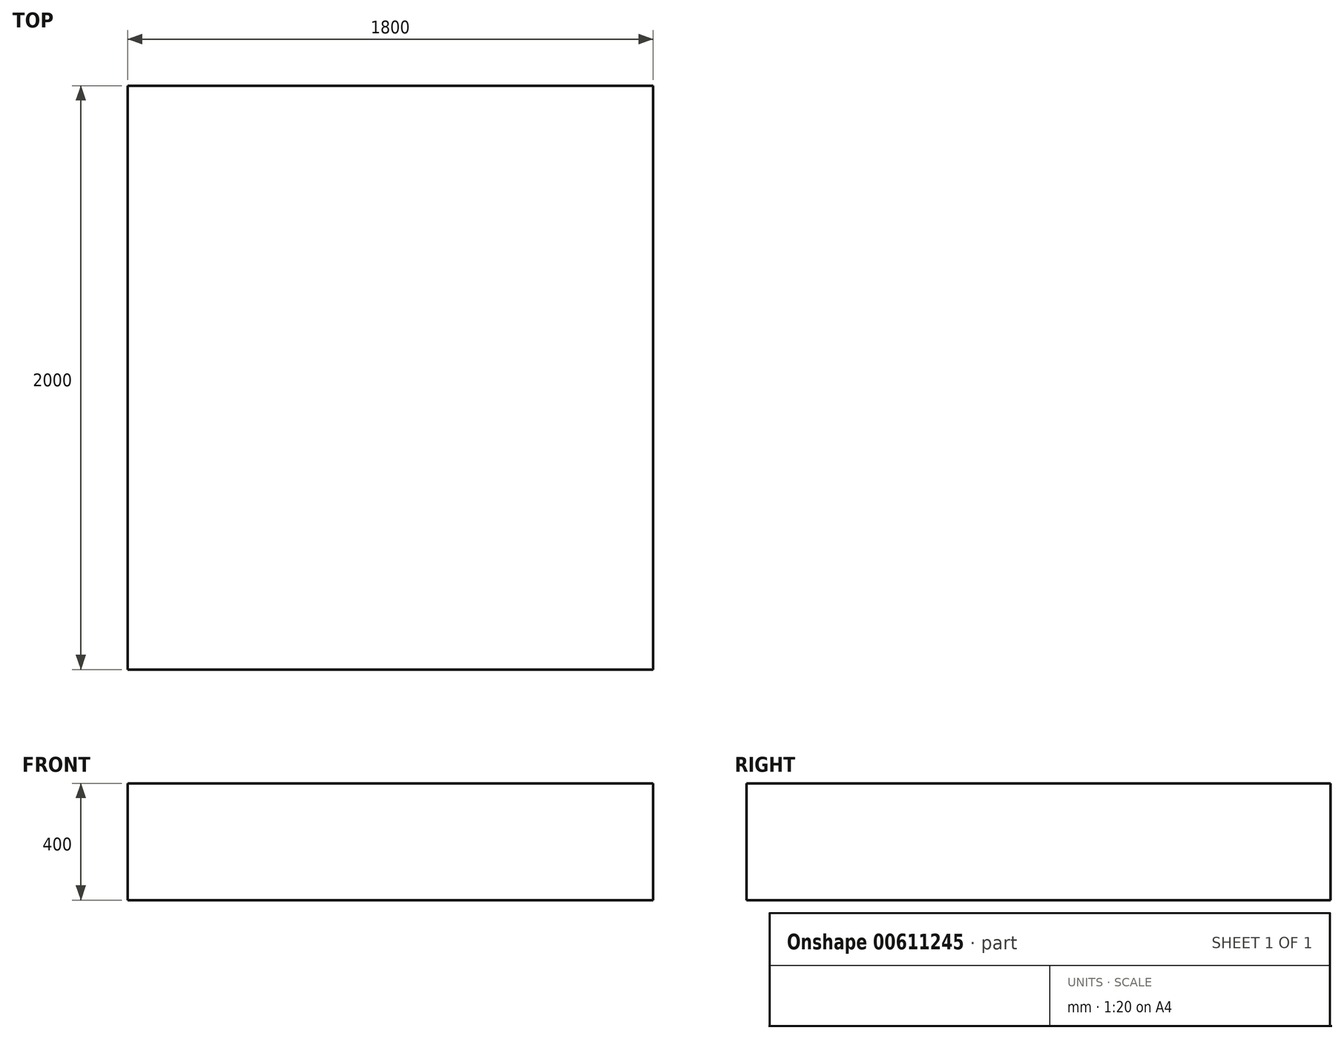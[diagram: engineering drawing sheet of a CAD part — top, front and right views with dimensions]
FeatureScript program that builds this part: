
annotation { "Feature Type Name" : "Feature", "Feature Type Description" : "" }
export const myFeature = defineFeature(function(context is Context, id is Id, definition is map)
    precondition{}
    {
        {
            var Q0;
            Q0=qCreatedBy(makeId("Top.planeOp"),FACE);
            var sketch = newSketch(context, id + "F0", { "sketchPlane" : qUnion([Q0])});
            skLineSegment(sketch, "E0.bottom", {"start": v(0, 0) * mm, "end": v(1800, 0) * mm});
            skLineSegment(sketch, "E0.top", {"start": v(0, 2000) * mm, "end": v(1800, 2000) * mm});
            skLineSegment(sketch, "E0.left", {"start": v(0, 0) * mm, "end": v(0, 2000) * mm});
            skLineSegment(sketch, "E0.right", {"start": v(1800, 0) * mm, "end": v(1800, 2000) * mm});
            skSolve(sketch);
        }
        {
            var Q0;
            Q0 = qSketchRegion(id + "F0", true);
            extrude(context, id + "F1", {"entities" : qUnion([Q0]), "depth" : 400 * mm, "offsetDistance" : 25 * mm});
        }
        {
            var Q0;
            Q0=qCreatedBy(makeId("Top.planeOp"),FACE);
            var sketch = newSketch(context, id + "F2", { "sketchPlane" : qUnion([Q0])});
            skLineSegment(sketch, "E1.bottom", {"start": v(50.84, 1944.82) * mm, "end": v(250.84, 1944.82) * mm});
            skLineSegment(sketch, "E1.top", {"start": v(50.84, 1744.82) * mm, "end": v(250.84, 1744.82) * mm});
            skLineSegment(sketch, "E1.left", {"start": v(50.84, 1944.82) * mm, "end": v(50.84, 1744.82) * mm});
            skLineSegment(sketch, "E1.right", {"start": v(250.84, 1944.82) * mm, "end": v(250.84, 1744.82) * mm});
            skLineSegment(sketch, "E2.bottom", {"start": v(1548.77, 1966.01) * mm, "end": v(1748.77, 1966.01) * mm});
            skLineSegment(sketch, "E2.top", {"start": v(1548.77, 1766.01) * mm, "end": v(1748.77, 1766.01) * mm});
            skLineSegment(sketch, "E2.left", {"start": v(1548.77, 1966.01) * mm, "end": v(1548.77, 1766.01) * mm});
            skLineSegment(sketch, "E2.right", {"start": v(1748.77, 1966.01) * mm, "end": v(1748.77, 1766.01) * mm});
            skLineSegment(sketch, "E3.bottom", {"start": v(111.26, 265.15) * mm, "end": v(311.26, 265.15) * mm});
            skLineSegment(sketch, "E3.top", {"start": v(111.26, 65.15) * mm, "end": v(311.26, 65.15) * mm});
            skLineSegment(sketch, "E3.left", {"start": v(111.26, 265.15) * mm, "end": v(111.26, 65.15) * mm});
            skLineSegment(sketch, "E3.right", {"start": v(311.26, 265.15) * mm, "end": v(311.26, 65.15) * mm});
            skLineSegment(sketch, "E4.bottom", {"start": v(1511.53, 312.61) * mm, "end": v(1711.53, 312.61) * mm});
            skLineSegment(sketch, "E4.top", {"start": v(1511.53, 112.61) * mm, "end": v(1711.53, 112.61) * mm});
            skLineSegment(sketch, "E4.left", {"start": v(1511.53, 312.61) * mm, "end": v(1511.53, 112.61) * mm});
            skLineSegment(sketch, "E4.right", {"start": v(1711.53, 312.61) * mm, "end": v(1711.53, 112.61) * mm});
            skSolve(sketch);
        }
        {
            var Q0;
            Q0=sQuery(id+"F2.wireOp",EDGE,"E3.top");
            var Q1;
            Q1=sQuery(id+"F2.wireOp",EDGE,"E3.bottom");
            var Q2;
            Q2=sQuery(id+"F2.wireOp",EDGE,"E3.left");
            var Q3;
            Q3=sQuery(id+"F2.wireOp",EDGE,"E3.right");
            var Q4;
            Q4=sQuery(id+"F2.wireOp",EDGE,"E1.bottom");
            var Q5;
            Q5=sQuery(id+"F2.wireOp",EDGE,"E1.right");
            var Q6;
            Q6=sQuery(id+"F2.wireOp",EDGE,"E1.top");
            var Q7;
            Q7=sQuery(id+"F2.wireOp",EDGE,"E1.left");
            var Q8;
            Q8=sQuery(id+"F2.wireOp",EDGE,"E2.left");
            var Q9;
            Q9=sQuery(id+"F2.wireOp",EDGE,"E2.bottom");
            var Q10;
            Q10=sQuery(id+"F2.wireOp",EDGE,"E2.right");
            var Q11;
            Q11=sQuery(id+"F2.wireOp",EDGE,"E2.top");
            var Q12;
            Q12=sQuery(id+"F2.wireOp",EDGE,"E4.bottom");
            var Q13;
            Q13=sQuery(id+"F2.wireOp",EDGE,"E4.right");
            var Q14;
            Q14=sQuery(id+"F2.wireOp",EDGE,"E4.top");
            var Q15;
            Q15=sQuery(id+"F2.wireOp",EDGE,"E4.left");
            extrude(context, id + "F3", {"bodyType" : ToolBodyType.SURFACE, "surfaceEntities" : qUnion([Q0, Q1, Q2, Q3, Q4, Q5, Q6, Q7, Q8, Q9, Q10, Q11, Q12, Q13, Q14, Q15]), "oppositeDirection" : true, "depth" : 150 * mm, "offsetDistance" : 25 * mm});
        }
    });
